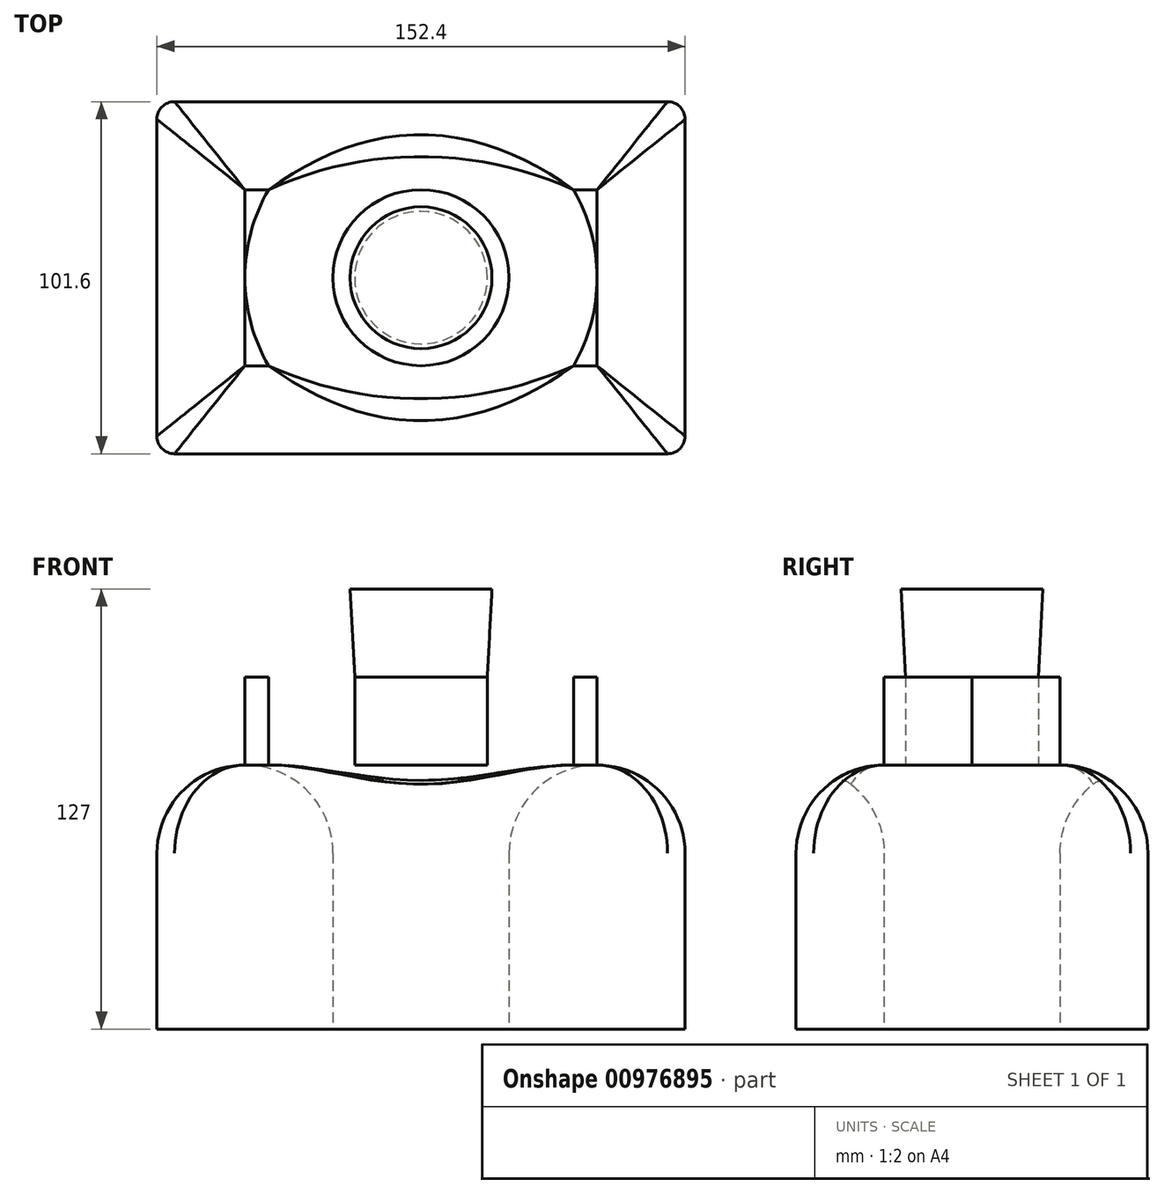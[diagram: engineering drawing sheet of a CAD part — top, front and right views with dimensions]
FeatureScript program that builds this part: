
annotation { "Feature Type Name" : "Feature", "Feature Type Description" : "" }
export const myFeature = defineFeature(function(context is Context, id is Id, definition is map)
    precondition{}
    {
        {
            var Q0;
            Q0=qCreatedBy(makeId("Top.planeOp"),FACE);
            var sketch = newSketch(context, id + "F0", { "sketchPlane" : qUnion([Q0])});
            skLineSegment(sketch, "E0.bottom", {"start": v(-76.2, 50.8) * mm, "end": v(76.2, 50.8) * mm});
            skLineSegment(sketch, "E0.top", {"start": v(-76.2, -50.8) * mm, "end": v(76.2, -50.8) * mm});
            skLineSegment(sketch, "E0.left", {"start": v(-76.2, 50.8) * mm, "end": v(-76.2, -50.8) * mm});
            skLineSegment(sketch, "E0.right", {"start": v(76.2, 50.8) * mm, "end": v(76.2, -50.8) * mm});
            skPoint(sketch, "E0.middle", {"position": v(0, 0) * mm});
            skCircle(sketch, "E1", {"center": v(0, 0) * mm, "radius": 25.4 * mm});
            skSolve(sketch);
        }
        {
            var Q0;
            Q0=makeQuery(id+"F0.imprint","IMPRINT",FACE,{"disambiguationData":[TD([[makeQuery(id+"F0.imprint","IMPRINT",EDGE,{"derivedFrom":sQuery(id+"F0.wireOp",EDGE,"E0.bottom")}),-1.0]])]});
            extrude(context, id + "F1", {"entities" : qUnion([Q0]), "depth" : 76.2 * mm, "offsetDistance" : 25.4 * mm});
        }
        {
            var Q0;
            Q0=makeQuery(id+"F1.opExtrude","CAP_FACE",FACE,{"disambiguationData":[OSD([sQuery(id+"F0.wireOp",EDGE,"E0.bottom"),sQuery(id+"F0.wireOp",EDGE,"E0.top"),sQuery(id+"F0.wireOp",EDGE,"E0.left"),sQuery(id+"F0.wireOp",EDGE,"E0.right"),sQuery(id+"F0.wireOp",EDGE,"E1")])],"isStart":false});
            var sketch = newSketch(context, id + "F2", { "sketchPlane" : qUnion([Q0])});
            skCircle(sketch, "E2", {"center": v(0, 0) * mm, "radius": 19.14 * mm});
            skLineSegment(sketch, "E3.bottom", {"start": v(43.56, 41.51) * mm, "end": v(73.63, 41.51) * mm});
            skLineSegment(sketch, "E3.top", {"start": v(43.56, 24.66) * mm, "end": v(73.63, 24.66) * mm});
            skLineSegment(sketch, "E3.left", {"start": v(43.56, 41.51) * mm, "end": v(43.56, 24.66) * mm});
            skLineSegment(sketch, "E3.right", {"start": v(73.63, 41.51) * mm, "end": v(73.63, 24.66) * mm});
            skSolve(sketch);
        }
        {
            var Q0;
            Q0=makeQuery(id+"F1.opExtrude","CAP_EDGE",EDGE,{"disambiguationData":[OSD([sQuery(id+"F0.wireOp",EDGE,"E0.bottom")])],"isStart":false});
            var Q1;
            Q1=makeQuery(id+"F1.opExtrude","CAP_FACE",FACE,{"disambiguationData":[OSD([sQuery(id+"F0.wireOp",EDGE,"E0.bottom"),sQuery(id+"F0.wireOp",EDGE,"E0.top"),sQuery(id+"F0.wireOp",EDGE,"E0.left"),sQuery(id+"F0.wireOp",EDGE,"E0.right"),sQuery(id+"F0.wireOp",EDGE,"E1")])],"isStart":false});
            fillet(context, id + "F3", {"entities" : qUnion([Q0, Q1]), "radius" : 25.4 * mm, "tangentPropagation" : true, "allowEdgeOverflow" : false});
        }
        {
            var Q0;
            Q0=makeQuery(id+"F2.imprint","IMPRINT",FACE,{"disambiguationData":[TD([[makeQuery(id+"F2.imprint","IMPRINT",EDGE,{"derivedFrom":sQuery(id+"F2.wireOp",EDGE,"E2")}),1.0]])]});
            extrude(context, id + "F4", {"entities" : qUnion([Q0]), "depth" : 25.4 * mm, "offsetDistance" : 25.4 * mm});
        }
        {
            var Q0;
            Q0=makeQuery(id+"F4.opExtrude","CAP_FACE",FACE,{"disambiguationData":[OSD([sQuery(id+"F2.wireOp",EDGE,"E2")])],"isStart":false});
            extrude(context, id + "F5", {"entities" : qUnion([Q0]), "depth" : 25.4 * mm, "offsetDistance" : 25.4 * mm, "hasDraft" : true, "draftAngle" : 3 * degree, "hasSecondDirectionDraft" : true, "secondDirectionDraftAngle" : 3 * degree});
        }
        {
            var Q0;
            Q0=makeQuery(id+"F3.opFillet","SPLIT",FACE,{"disambiguationData":[OD(1.0)],"derivedFrom":makeQuery(id+"F1.opExtrude","CAP_FACE",FACE,{"disambiguationData":[OSD([sQuery(id+"F0.wireOp",EDGE,"E0.bottom"),sQuery(id+"F0.wireOp",EDGE,"E0.top"),sQuery(id+"F0.wireOp",EDGE,"E0.left"),sQuery(id+"F0.wireOp",EDGE,"E0.right"),sQuery(id+"F0.wireOp",EDGE,"E1")])],"isStart":false})});
            var Q1;
            Q1=makeQuery(id+"F3.opFillet","SPLIT",FACE,{"disambiguationData":[OD(0.0)],"derivedFrom":makeQuery(id+"F1.opExtrude","CAP_FACE",FACE,{"disambiguationData":[OSD([sQuery(id+"F0.wireOp",EDGE,"E0.bottom"),sQuery(id+"F0.wireOp",EDGE,"E0.top"),sQuery(id+"F0.wireOp",EDGE,"E0.left"),sQuery(id+"F0.wireOp",EDGE,"E0.right"),sQuery(id+"F0.wireOp",EDGE,"E1")])],"isStart":false})});
            var Q2;
            Q2=makeQuery(id+"F3.opFillet","SPLIT",FACE,{"disambiguationData":[OD(2.0)],"derivedFrom":makeQuery(id+"F1.opExtrude","CAP_FACE",FACE,{"disambiguationData":[OSD([sQuery(id+"F0.wireOp",EDGE,"E0.bottom"),sQuery(id+"F0.wireOp",EDGE,"E0.top"),sQuery(id+"F0.wireOp",EDGE,"E0.left"),sQuery(id+"F0.wireOp",EDGE,"E0.right"),sQuery(id+"F0.wireOp",EDGE,"E1")])],"isStart":false})});
            var Q3;
            Q3=makeQuery(id+"F3.opFillet","SPLIT",FACE,{"disambiguationData":[OD(3.0)],"derivedFrom":makeQuery(id+"F1.opExtrude","CAP_FACE",FACE,{"disambiguationData":[OSD([sQuery(id+"F0.wireOp",EDGE,"E0.bottom"),sQuery(id+"F0.wireOp",EDGE,"E0.top"),sQuery(id+"F0.wireOp",EDGE,"E0.left"),sQuery(id+"F0.wireOp",EDGE,"E0.right"),sQuery(id+"F0.wireOp",EDGE,"E1")])],"isStart":false})});
            extrude(context, id + "F6", {"entities" : qUnion([Q0, Q1, Q2, Q3]), "depth" : 25.4 * mm, "offsetDistance" : 25.4 * mm});
        }
        {
            var Q0;
            Q0=makeQuery(id+"F3.opFillet","BLEND_FACE",FACE,{"disambiguationData":[OSD([sQuery(id+"F0.wireOp",EDGE,"E0.bottom")])]});
            var Q1;
            Q1=makeQuery(id+"F3.opFillet","BLEND_FACE",FACE,{"disambiguationData":[OSD([sQuery(id+"F0.wireOp",EDGE,"E0.left")])]});
            var Q2;
            Q2=makeQuery(id+"F3.opFillet","BLEND_FACE",FACE,{"disambiguationData":[OSD([sQuery(id+"F0.wireOp",EDGE,"E0.top")])]});
            var Q3;
            Q3=makeQuery(id+"F3.opFillet","BLEND_FACE",FACE,{"disambiguationData":[OSD([sQuery(id+"F0.wireOp",EDGE,"E0.right")])]});
            fillet(context, id + "F7", {"entities" : qUnion([Q0, Q1, Q2, Q3]), "radius" : 5.08 * mm, "tangentPropagation" : true, "allowEdgeOverflow" : false});
        }
    });
